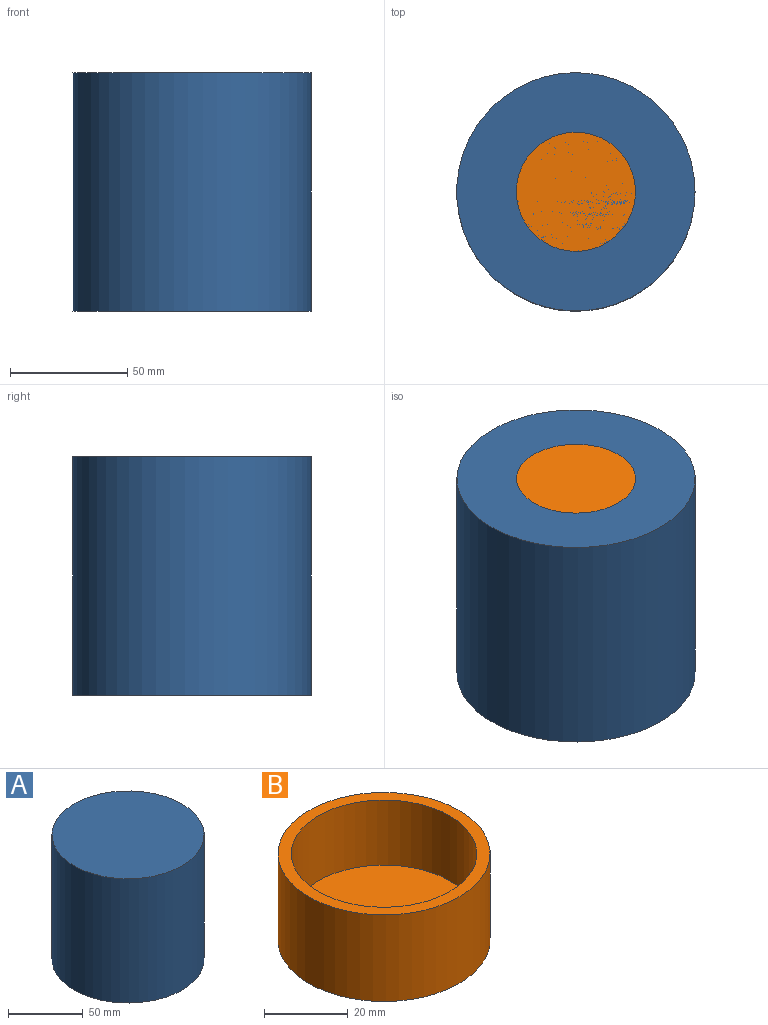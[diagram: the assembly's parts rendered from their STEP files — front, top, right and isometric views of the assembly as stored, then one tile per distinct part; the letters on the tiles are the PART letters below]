
ASSEMBLY  parts=2 mates=1
PART A: 5 faces, bbox 101.6x101.6x101.6 mm
  f0: cylinder r=50.8mm len=101.6mm, axis (0,0,-1), area 32429.3mm2, adj f1,f2
  f1: plane 101.6x101.6mm, normal (0,0,1), area 8107.3mm2, adj f0
  f2: plane 101.6x101.6mm, normal (0,0,-1), area 981.7mm2, adj f0,f3
  f3: cylinder r=47.62mm len=95.25mm, axis (0,0,-1), area 28502.3mm2, adj f2,f4
  f4: plane 95.25x95.25mm, normal (0,0,-1), area 7125.6mm2, adj f3
PART B: 5 faces, bbox 50.8x50.8x25.4 mm
  f0: cylinder r=22.23mm len=44.45mm, axis (0,0,-1), area 2660.2mm2, adj f2,f4
  f1: cylinder r=25.4mm len=50.8mm, axis (0,0,-1), area 4053.7mm2, adj f2,f3
  f2: plane 50.8x50.8mm, normal (0,0,1), area 475mm2, adj f0,f1
  f3: plane 50.8x50.8mm, normal (0,0,-1), area 2026.8mm2, adj f1
  f4: plane 44.45x44.45mm, normal (0,0,1), area 1551.8mm2, adj f0
PLACE A t=(-32.18,51.49,8.19)mm
PLACE B rot(axis=(1,0,0),180deg) t=(-74.5,78.46,109.79)mm
MATE slider B.f0 <-> A.f0  axis (0,0,-1) through (-74.5,78.46,103.44)mm
